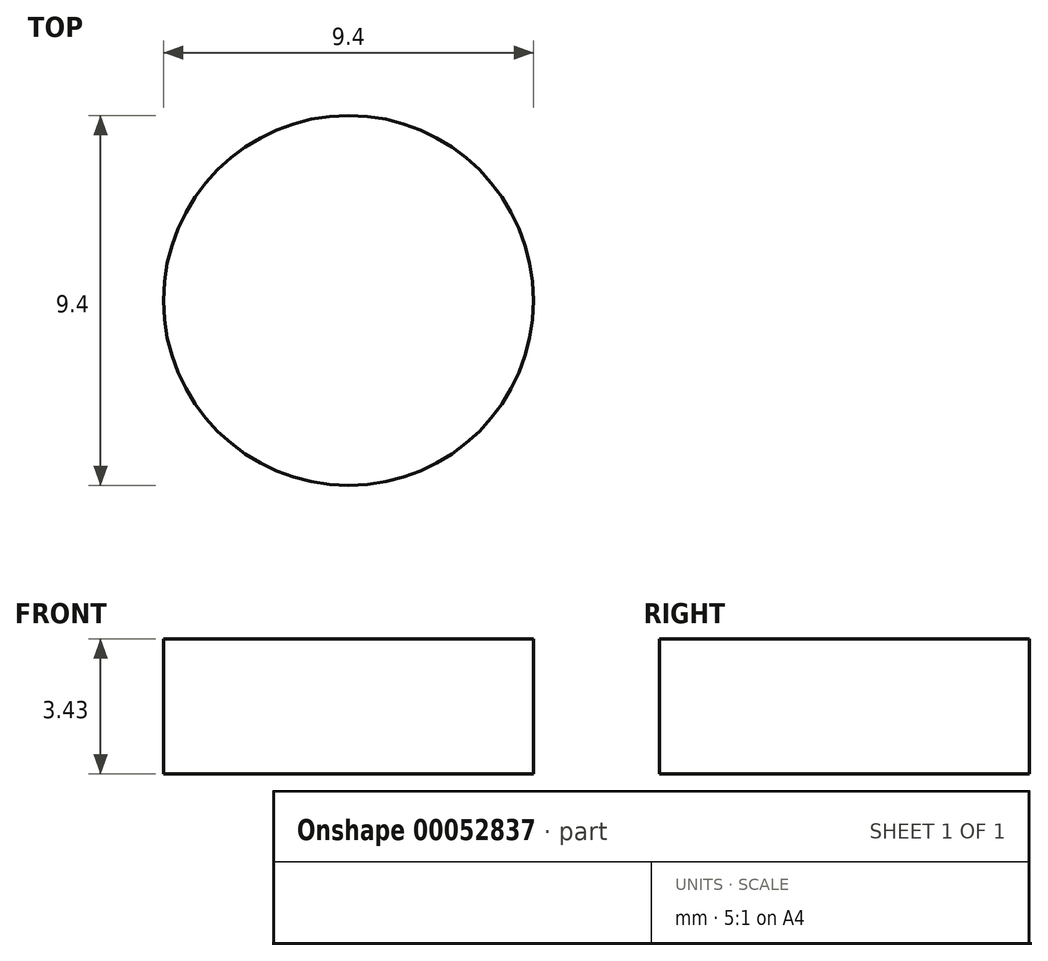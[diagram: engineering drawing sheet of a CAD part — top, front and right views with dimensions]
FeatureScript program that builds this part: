
annotation { "Feature Type Name" : "Feature", "Feature Type Description" : "" }
export const myFeature = defineFeature(function(context is Context, id is Id, definition is map)
    precondition{}
    {
        {
            var Q0;
            Q0=qCreatedBy(makeId("Top.planeOp"),FACE);
            var sketch = newSketch(context, id + "F0", { "sketchPlane" : qUnion([Q0])});
            skCircle(sketch, "E0", {"center": v(0, 0) * mm, "radius": 4.7 * mm});
            skSolve(sketch);
        }
        {
            var Q0;
            Q0=qSketchRegion(id+"F0",true);
            extrude(context, id + "F1", {"entities" : qUnion([Q0]), "depth" : 3.43 * mm});
        }
    });
